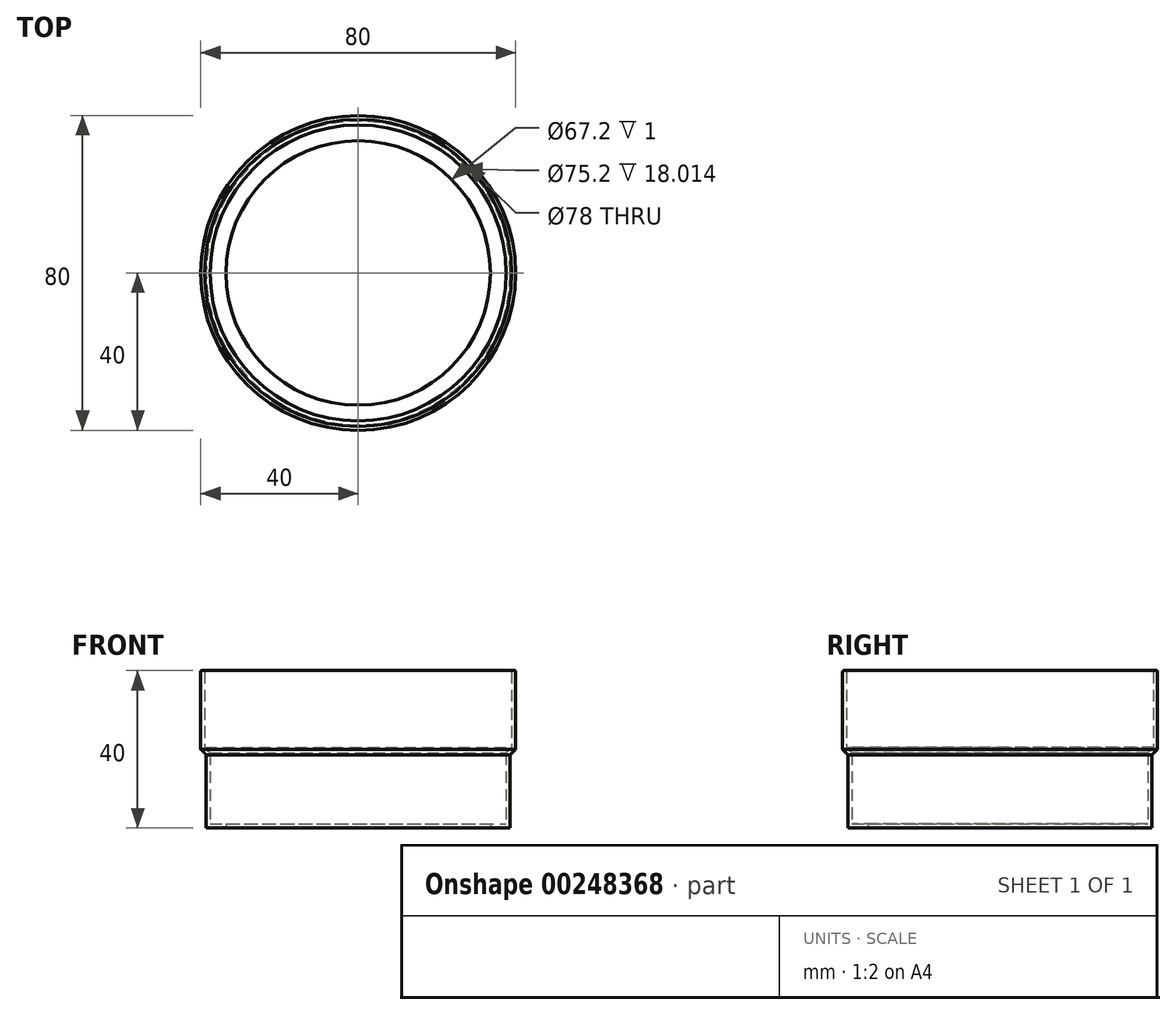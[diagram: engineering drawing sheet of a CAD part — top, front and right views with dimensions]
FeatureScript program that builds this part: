
annotation { "Feature Type Name" : "Feature", "Feature Type Description" : "" }
export const myFeature = defineFeature(function(context is Context, id is Id, definition is map)
    precondition{}
    {
        {
            var Q0;
            Q0=qCreatedBy(makeId("Front.planeOp"),FACE);
            var sketch = newSketch(context, id + "F0", { "sketchPlane" : qUnion([Q0])});
            skLineSegment(sketch, "E0", {"start": v(-40, 38.02) * mm, "end": v(-40, 18.32) * mm});
            skLineSegment(sketch, "E1", {"start": v(-40, 18.32) * mm, "end": v(-40, 16.92) * mm, "construction": true});
            skLineSegment(sketch, "E2", {"start": v(-40, 16.92) * mm, "end": v(-38.6, 16.92) * mm, "construction": true});
            skLineSegment(sketch, "E3", {"start": v(-38.6, 16.92) * mm, "end": v(-38.6, -1.68) * mm});
            skLineSegment(sketch, "E4", {"start": v(-38.6, -1.68) * mm, "end": v(-33.6, -1.68) * mm});
            skLineSegment(sketch, "E5", {"start": v(-37.6, -0.68) * mm, "end": v(-37.6, 17.33) * mm});
            skLineSegment(sketch, "E6", {"start": v(-39, 18.73) * mm, "end": v(-39, 38.02) * mm});
            skLineSegment(sketch, "E7", {"start": v(-39.3, 38.32) * mm, "end": v(-39.7, 38.32) * mm});
            skLineSegment(sketch, "E8", {"start": v(-40, 18.32) * mm, "end": v(-38.6, 16.92) * mm});
            skLineSegment(sketch, "E9", {"start": v(-37.6, -0.68) * mm, "end": v(-33.6, -0.68) * mm});
            skLineSegment(sketch, "E10", {"start": v(-33.6, -0.68) * mm, "end": v(-33.6, -1.68) * mm});
            skLineSegment(sketch, "E11", {"start": v(-39, 18.73) * mm, "end": v(-37.6, 17.33) * mm});
            skLineSegment(sketch, "E12", {"start": v(0, 0) * mm, "end": v(0, 12.27) * mm, "construction": true});
            skPoint(sketch, "E13.visualSharp", {"position": v(-40, 38.32) * mm});
            skArc(sketch, "E13.filletArc", {"start": v(-39.7, 38.32) * mm, "mid": v(-39.91, 38.23) * mm, "end": v(-40, 38.02) * mm});
            skPoint(sketch, "E14.visualSharp", {"position": v(-39, 38.32) * mm});
            skArc(sketch, "E14.filletArc", {"start": v(-39, 38.02) * mm, "mid": v(-39.09, 38.23) * mm, "end": v(-39.3, 38.32) * mm});
            skSolve(sketch);
        }
        {
            var Q0;
            Q0 = qSketchRegion(id + "F0", true);
            var Q1;
            Q1=sQuery(id+"F0.wireOp",EDGE,"E12");
            revolve(context, id + "F1", {"entities" : qUnion([Q0]), "axis" : qUnion([Q1]), "revolveType" : RevolveType.FULL});
        }
    });
